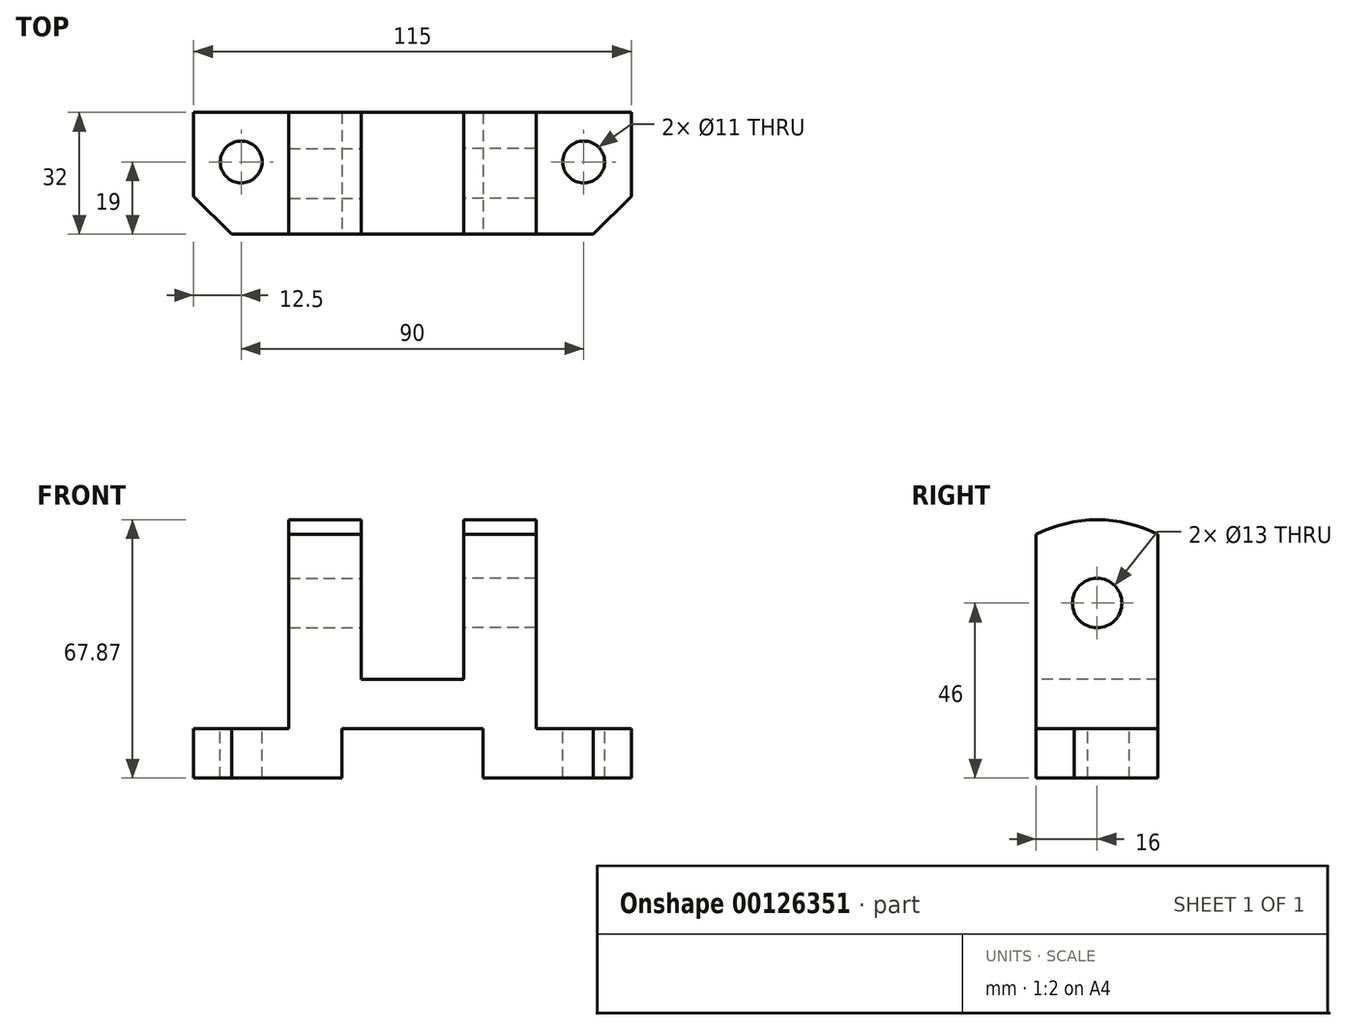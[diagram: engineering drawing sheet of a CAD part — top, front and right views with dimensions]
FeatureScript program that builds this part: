
annotation { "Feature Type Name" : "Feature", "Feature Type Description" : "" }
export const myFeature = defineFeature(function(context is Context, id is Id, definition is map)
    precondition{}
    {
        {
            var Q0;
            Q0=qCreatedBy(makeId("Front.planeOp"),FACE);
            var sketch = newSketch(context, id + "F0", { "sketchPlane" : qUnion([Q0])});
            skLineSegment(sketch, "E0", {"start": v(-57.5, -13) * mm, "end": v(-18.5, -13) * mm});
            skLineSegment(sketch, "E1", {"start": v(-18.5, -13) * mm, "end": v(-18.5, 0) * mm});
            skLineSegment(sketch, "E2", {"start": v(-57.5, -13) * mm, "end": v(-57.5, 0) * mm});
            skLineSegment(sketch, "E3", {"start": v(-57.5, 0) * mm, "end": v(-32.5, 0) * mm});
            skLineSegment(sketch, "E4", {"start": v(-32.5, 0) * mm, "end": v(-32.5, 51) * mm});
            skLineSegment(sketch, "E5", {"start": v(-32.5, 51) * mm, "end": v(-13.5, 51) * mm});
            skLineSegment(sketch, "E6", {"start": v(-13.5, 51) * mm, "end": v(-13.5, 13) * mm});
            skLineSegment(sketch, "E7", {"start": v(-13.5, 13) * mm, "end": v(0, 13) * mm});
            skLineSegment(sketch, "E8", {"start": v(0, 13) * mm, "end": v(0, 0) * mm});
            skLineSegment(sketch, "E9", {"start": v(-47.5, -13) * mm, "end": v(-47.5, 0) * mm});
            skLineSegment(sketch, "E10", {"start": v(0, 0) * mm, "end": v(-18.5, 0) * mm});
            skSolve(sketch);
        }
        {
            var Q0;
            Q0 = qSketchRegion(id + "F0", true);
            extrude(context, id + "F1", {"entities" : qUnion([Q0]), "oppositeDirection" : true, "depth" : 32 * mm});
        }
        {
            var Q0;
            Q0=makeQuery(id+"F1.opExtrude","SWEPT_FACE",FACE,{"disambiguationData":[OSD([sQuery(id+"F0.wireOp",EDGE,"E3")])]});
            var sketch = newSketch(context, id + "F2", { "sketchPlane" : qUnion([Q0])});
            skCircle(sketch, "E11", {"center": v(-45, 19) * mm, "radius": 5.5 * mm});
            skLineSegment(sketch, "E12", {"start": v(-47.5, 0) * mm, "end": v(-57.5, 10) * mm});
            skLineSegment(sketch, "E13", {"start": v(-47.5, 0) * mm, "end": v(-57.5, 0) * mm});
            skLineSegment(sketch, "E14", {"start": v(-57.5, 0) * mm, "end": v(-57.5, 10) * mm});
            skSolve(sketch);
        }
        {
            var Q0;
            Q0 = qSketchRegion(id + "F2", true);
            extrude(context, id + "F3", {"entities" : qUnion([Q0]), "operationType" : NewBodyOperationType.REMOVE, "oppositeDirection" : true, "depth" : 25 * mm});
        }
        {
            var Q0;
            Q0=makeQuery(id+"F1.opExtrude","SWEPT_FACE",FACE,{"disambiguationData":[OSD([sQuery(id+"F0.wireOp",EDGE,"E6")])]});
            var sketch = newSketch(context, id + "F4", { "sketchPlane" : qUnion([Q0])});
            skCircle(sketch, "E15", {"center": v(16, 33) * mm, "radius": 6.5 * mm});
            skSolve(sketch);
        }
        {
            var Q0;
            Q0 = qSketchRegion(id + "F4", true);
            extrude(context, id + "F5", {"entities" : qUnion([Q0]), "operationType" : NewBodyOperationType.REMOVE, "oppositeDirection" : true, "depth" : 25 * mm});
        }
        {
            var Q0;
            Q0=makeQuery(id+"F1.opExtrude","SWEPT_FACE",FACE,{"disambiguationData":[OSD([sQuery(id+"F0.wireOp",EDGE,"E6")])]});
            var sketch = newSketch(context, id + "F6", { "sketchPlane" : qUnion([Q0])});
            skArc(sketch, "E16", {"start": v(32, 51) * mm, "mid": v(16, 54.87) * mm, "end": v(0, 51) * mm});
            skLineSegment(sketch, "E17", {"start": v(0, 51) * mm, "end": v(32, 51) * mm});
            skSolve(sketch);
        }
        {
            var Q0;
            Q0 = qSketchRegion(id + "F6", true);
            extrude(context, id + "F7", {"entities" : qUnion([Q0]), "operationType" : NewBodyOperationType.ADD, "oppositeDirection" : true, "depth" : 19 * mm});
        }
        {
            var Q0;
            Q0=makeQuery(id+"F1.opExtrude","SWEPT_BODY",BODY,{"disambiguationData":[OSD([sQuery(id+"F0.wireOp",EDGE,"E0"),sQuery(id+"F0.wireOp",EDGE,"E1"),sQuery(id+"F0.wireOp",EDGE,"E2"),sQuery(id+"F0.wireOp",EDGE,"E3"),sQuery(id+"F0.wireOp",EDGE,"E4"),sQuery(id+"F0.wireOp",EDGE,"E5"),sQuery(id+"F0.wireOp",EDGE,"E6"),sQuery(id+"F0.wireOp",EDGE,"E7"),sQuery(id+"F0.wireOp",EDGE,"E8"),sQuery(id+"F0.wireOp",EDGE,"E10")])]});
            var Q1;
            Q1=qCreatedBy(makeId("Right.planeOp"),FACE);
            mirror(context, id + "F8", {"operationType" : NewBodyOperationType.ADD, "entities" : qUnion([Q0]), "mirrorPlane" : qUnion([Q1])});
        }
    });
